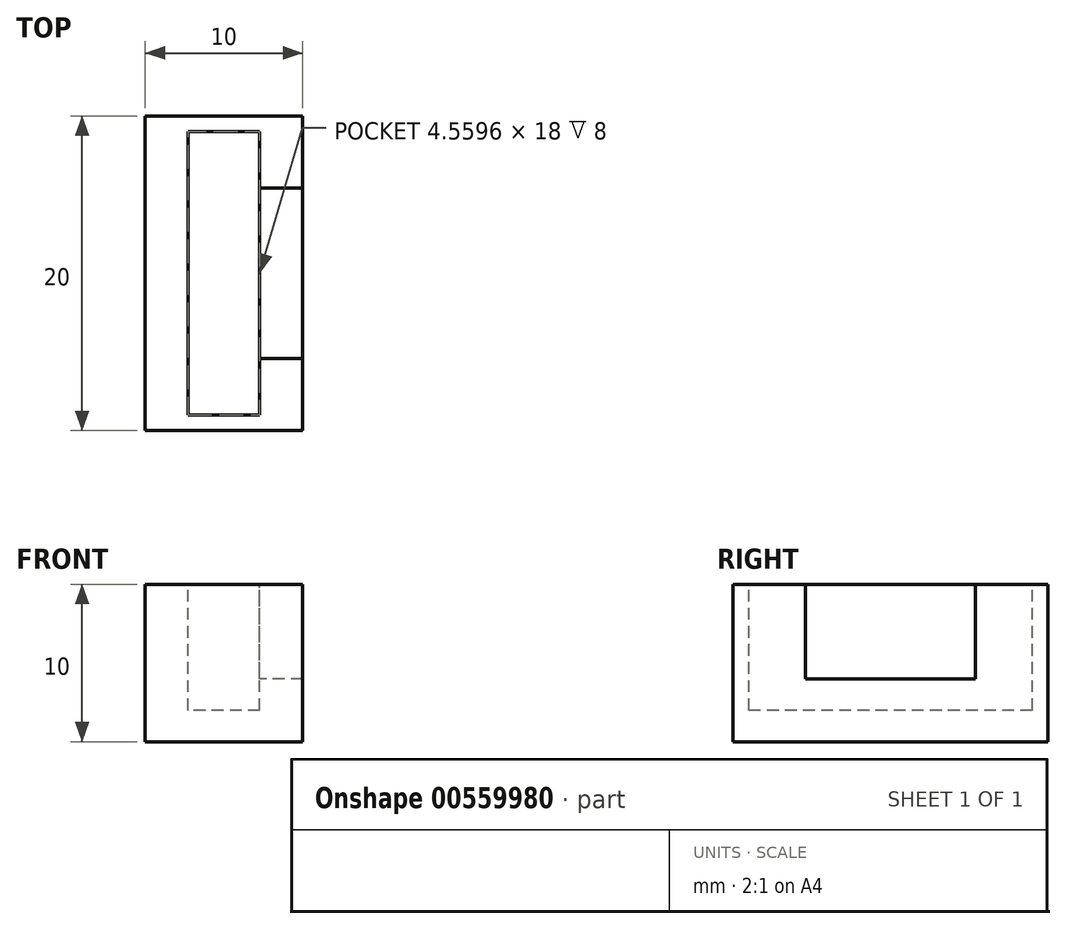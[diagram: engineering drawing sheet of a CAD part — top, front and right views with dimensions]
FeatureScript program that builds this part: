
annotation { "Feature Type Name" : "Feature", "Feature Type Description" : "" }
export const myFeature = defineFeature(function(context is Context, id is Id, definition is map)
    precondition{}
    {
        {
            var Q0;
            Q0=qCreatedBy(makeId("Top.planeOp"),FACE);
            var sketch = newSketch(context, id + "F0", { "sketchPlane" : qUnion([Q0])});
            skLineSegment(sketch, "E0.bottom", {"start": v(5, 10) * mm, "end": v(-5, 10) * mm});
            skLineSegment(sketch, "E0.top", {"start": v(5, -10) * mm, "end": v(-5, -10) * mm});
            skLineSegment(sketch, "E0.left", {"start": v(5, 10) * mm, "end": v(5, -10) * mm});
            skLineSegment(sketch, "E0.right", {"start": v(-5, 10) * mm, "end": v(-5, -10) * mm});
            skPoint(sketch, "E0.middle", {"position": v(0, 0) * mm});
            skSolve(sketch);
        }
        {
            var Q0;
            Q0 = qSketchRegion(id + "F0", true);
            extrude(context, id + "F1", {"entities" : qUnion([Q0]), "depth" : 10 * mm, "offsetDistance" : 25 * mm});
        }
        {
            var Q0;
            Q0=makeQuery(id+"F1.opExtrude","CAP_FACE",FACE,{"disambiguationData":[OSD([sQuery(id+"F0.wireOp",EDGE,"E0.bottom"),sQuery(id+"F0.wireOp",EDGE,"E0.top"),sQuery(id+"F0.wireOp",EDGE,"E0.left"),sQuery(id+"F0.wireOp",EDGE,"E0.right")])],"isStart":false});
            var sketch = newSketch(context, id + "F2", { "sketchPlane" : qUnion([Q0])});
            skLineSegment(sketch, "E1.bottom", {"start": v(2.28, 9) * mm, "end": v(-2.28, 9) * mm});
            skLineSegment(sketch, "E1.top", {"start": v(2.28, -9) * mm, "end": v(-2.28, -9) * mm});
            skLineSegment(sketch, "E1.left", {"start": v(2.28, 9) * mm, "end": v(2.28, -9) * mm});
            skLineSegment(sketch, "E1.right", {"start": v(-2.28, 9) * mm, "end": v(-2.28, -9) * mm});
            skPoint(sketch, "E1.middle", {"position": v(0, 0) * mm});
            skLineSegment(sketch, "E2.left", {"start": v(5, 5.4) * mm, "end": v(5, -5.4) * mm});
            skPoint(sketch, "E2.middle", {"position": v(3.73, 0) * mm});
            skPoint(sketch, "E2.middle.positionSnap0", {"position": v(2.28, 0) * mm});
            skPoint(sketch, "E2.centerSnap0", {"position": v(2.28, 0) * mm});
            skLineSegment(sketch, "E3", {"start": v(5, -5.4) * mm, "end": v(2.28, -5.4) * mm});
            skLineSegment(sketch, "E4", {"start": v(5, 5.4) * mm, "end": v(2.28, 5.4) * mm});
            skLineSegment(sketch, "E5", {"start": v(2.28, 5.4) * mm, "end": v(2.28, -5.4) * mm});
            skSolve(sketch);
        }
        {
            var Q0;
            Q0=makeQuery(id+"F2.imprint","IMPRINT",FACE,{"disambiguationData":[TD([[makeQuery(id+"F2.imprint","IMPRINT",EDGE,{"derivedFrom":sQuery(id+"F2.wireOp",EDGE,"E1.bottom")}),1.0]])]});
            extrude(context, id + "F3", {"entities" : qUnion([Q0]), "operationType" : NewBodyOperationType.REMOVE, "oppositeDirection" : true, "depth" : 8 * mm, "offsetDistance" : 25 * mm});
        }
        {
            var Q0;
            Q0=makeQuery(id+"F2.imprint","IMPRINT",FACE,{"disambiguationData":[TD([[makeQuery(id+"F2.imprint","IMPRINT",EDGE,{"derivedFrom":sQuery(id+"F2.wireOp",EDGE,"E2.left")}),-1.0]])]});
            extrude(context, id + "F4", {"entities" : qUnion([Q0]), "operationType" : NewBodyOperationType.REMOVE, "oppositeDirection" : true, "depth" : 6 * mm, "offsetDistance" : 25 * mm});
        }
    });
